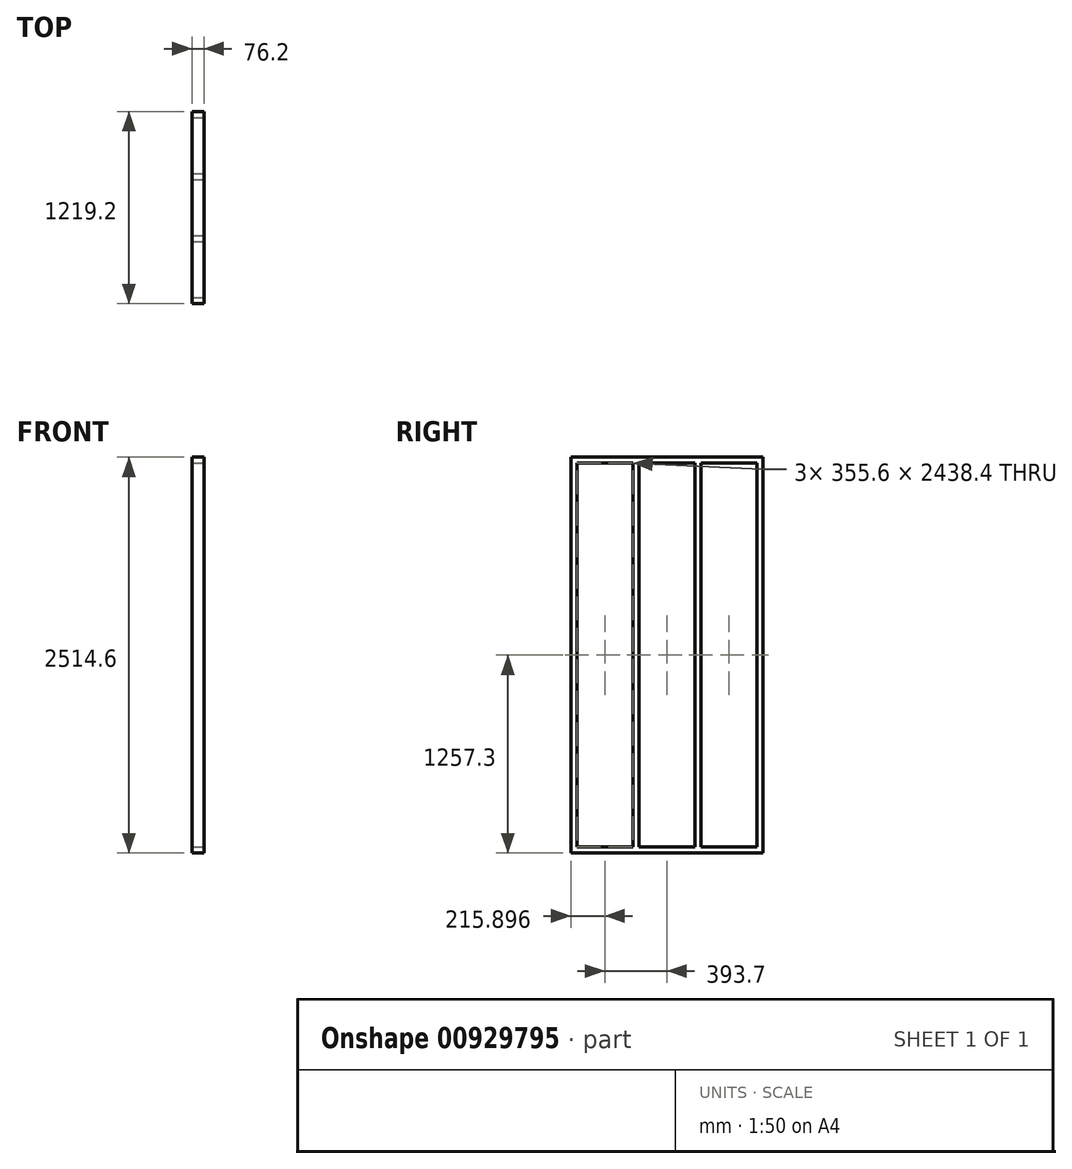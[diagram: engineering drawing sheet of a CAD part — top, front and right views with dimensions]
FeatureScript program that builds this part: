
annotation { "Feature Type Name" : "Feature", "Feature Type Description" : "" }
export const myFeature = defineFeature(function(context is Context, id is Id, definition is map)
    precondition{}
    {
        {
            var Q0;
            Q0=qCreatedBy(makeId("Top.planeOp"),FACE);
            var sketch = newSketch(context, id + "F0", { "sketchPlane" : qUnion([Q0])});
            skLineSegment(sketch, "E0.bottom", {"start": v(-41.18, -626) * mm, "end": v(-117.38, -626) * mm});
            skLineSegment(sketch, "E0.top", {"start": v(-41.18, 593.2) * mm, "end": v(-117.38, 593.2) * mm});
            skLineSegment(sketch, "E0.left", {"start": v(-41.18, -626) * mm, "end": v(-41.18, 593.2) * mm});
            skLineSegment(sketch, "E0.right", {"start": v(-117.38, -626) * mm, "end": v(-117.38, 593.2) * mm});
            skSolve(sketch);
        }
        {
            var Q0;
            Q0 = qSketchRegion(id + "F0", true);
            extrude(context, id + "F1", {"entities" : qUnion([Q0]), "depth" : 38.1 * mm, "offsetDistance" : 25.4 * mm});
        }
        {
            var Q0;
            Q0=makeQuery(id+"F1.opExtrude","CAP_FACE",FACE,{"disambiguationData":[OSD([sQuery(id+"F0.wireOp",EDGE,"E0.bottom"),sQuery(id+"F0.wireOp",EDGE,"E0.top"),sQuery(id+"F0.wireOp",EDGE,"E0.left"),sQuery(id+"F0.wireOp",EDGE,"E0.right")])],"isStart":false});
            var sketch = newSketch(context, id + "F2", { "sketchPlane" : qUnion([Q0])});
            skLineSegment(sketch, "E1.bottom", {"start": v(-117.38, -626) * mm, "end": v(-41.18, -626) * mm});
            skLineSegment(sketch, "E1.top", {"start": v(-117.38, -587.9) * mm, "end": v(-41.18, -587.9) * mm});
            skLineSegment(sketch, "E1.left", {"start": v(-117.38, -626) * mm, "end": v(-117.38, -587.9) * mm});
            skLineSegment(sketch, "E1.right", {"start": v(-41.18, -626) * mm, "end": v(-41.18, -587.9) * mm});
            skLineSegment(sketch, "E2.bottom", {"start": v(-117.38, 593.2) * mm, "end": v(-41.18, 593.2) * mm});
            skLineSegment(sketch, "E2.top", {"start": v(-117.38, 555.1) * mm, "end": v(-41.18, 555.1) * mm});
            skLineSegment(sketch, "E2.left", {"start": v(-117.38, 593.2) * mm, "end": v(-117.38, 555.1) * mm});
            skLineSegment(sketch, "E2.right", {"start": v(-41.18, 593.2) * mm, "end": v(-41.18, 555.1) * mm});
            skLineSegment(sketch, "E3.bottom", {"start": v(-117.38, 199.5) * mm, "end": v(-41.18, 199.5) * mm});
            skLineSegment(sketch, "E3.top", {"start": v(-117.38, 161.4) * mm, "end": v(-41.18, 161.4) * mm});
            skLineSegment(sketch, "E3.left", {"start": v(-117.38, 199.5) * mm, "end": v(-117.38, 161.4) * mm});
            skLineSegment(sketch, "E3.right", {"start": v(-41.18, 199.5) * mm, "end": v(-41.18, 161.4) * mm});
            skLineSegment(sketch, "E4.bottom", {"start": v(-117.38, -194.2) * mm, "end": v(-41.18, -194.2) * mm});
            skLineSegment(sketch, "E4.top", {"start": v(-117.38, -232.3) * mm, "end": v(-41.18, -232.3) * mm});
            skLineSegment(sketch, "E4.left", {"start": v(-117.38, -194.2) * mm, "end": v(-117.38, -232.3) * mm});
            skLineSegment(sketch, "E4.right", {"start": v(-41.18, -194.2) * mm, "end": v(-41.18, -232.3) * mm});
            skLineSegment(sketch, "E5", {"start": v(-79.28, 199.5) * mm, "end": v(-79.28, 555.1) * mm, "construction": true});
            skLineSegment(sketch, "E6", {"start": v(-79.28, 161.4) * mm, "end": v(-79.28, -194.2) * mm, "construction": true});
            skLineSegment(sketch, "E7", {"start": v(-79.28, -232.3) * mm, "end": v(-79.28, -587.9) * mm, "construction": true});
            skSolve(sketch);
        }
        {
            var Q0;
            Q0 = qSketchRegion(id + "F2", true);
            extrude(context, id + "F3", {"entities" : qUnion([Q0]), "operationType" : NewBodyOperationType.ADD, "depth" : 2438.4 * mm, "offsetDistance" : 25.4 * mm});
        }
        {
            var Q0;
            Q0 = qSketchRegion(id + "F0", true);
            var Q1;
            Q1=makeQuery(id+"F3.opExtrude","CAP_FACE",FACE,{"disambiguationData":[OSD([sQuery(id+"F2.wireOp",EDGE,"E4.bottom"),sQuery(id+"F2.wireOp",EDGE,"E4.top"),sQuery(id+"F2.wireOp",EDGE,"E4.left"),sQuery(id+"F2.wireOp",EDGE,"E4.right")])],"isStart":false});
            var Q2;
            Q2=makeQuery(id+"F3.opExtrude","CAP_FACE",FACE,{"disambiguationData":[OSD([sQuery(id+"F2.wireOp",EDGE,"E4.bottom"),sQuery(id+"F2.wireOp",EDGE,"E4.top"),sQuery(id+"F2.wireOp",EDGE,"E4.left"),sQuery(id+"F2.wireOp",EDGE,"E4.right")])],"isStart":false});
            extrude(context, id + "F4", {"entities" : qUnion([Q0]), "operationType" : NewBodyOperationType.ADD, "endBound" : BoundingType.UP_TO_SURFACE, "depth" : 25.4 * mm, "endBoundEntityFace" : qUnion([Q1]), "hasOffset" : true, "offsetDistance" : 38.1 * mm, "offsetOppositeDirection" : true, "hasSecondDirection" : true, "secondDirectionBound" : SecondDirectionBoundingType.UP_TO_SURFACE, "secondDirectionOppositeDirection" : false, "secondDirectionDepth" : 25.4 * mm, "secondDirectionBoundEntityFace" : qUnion([Q2])});
        }
    });
